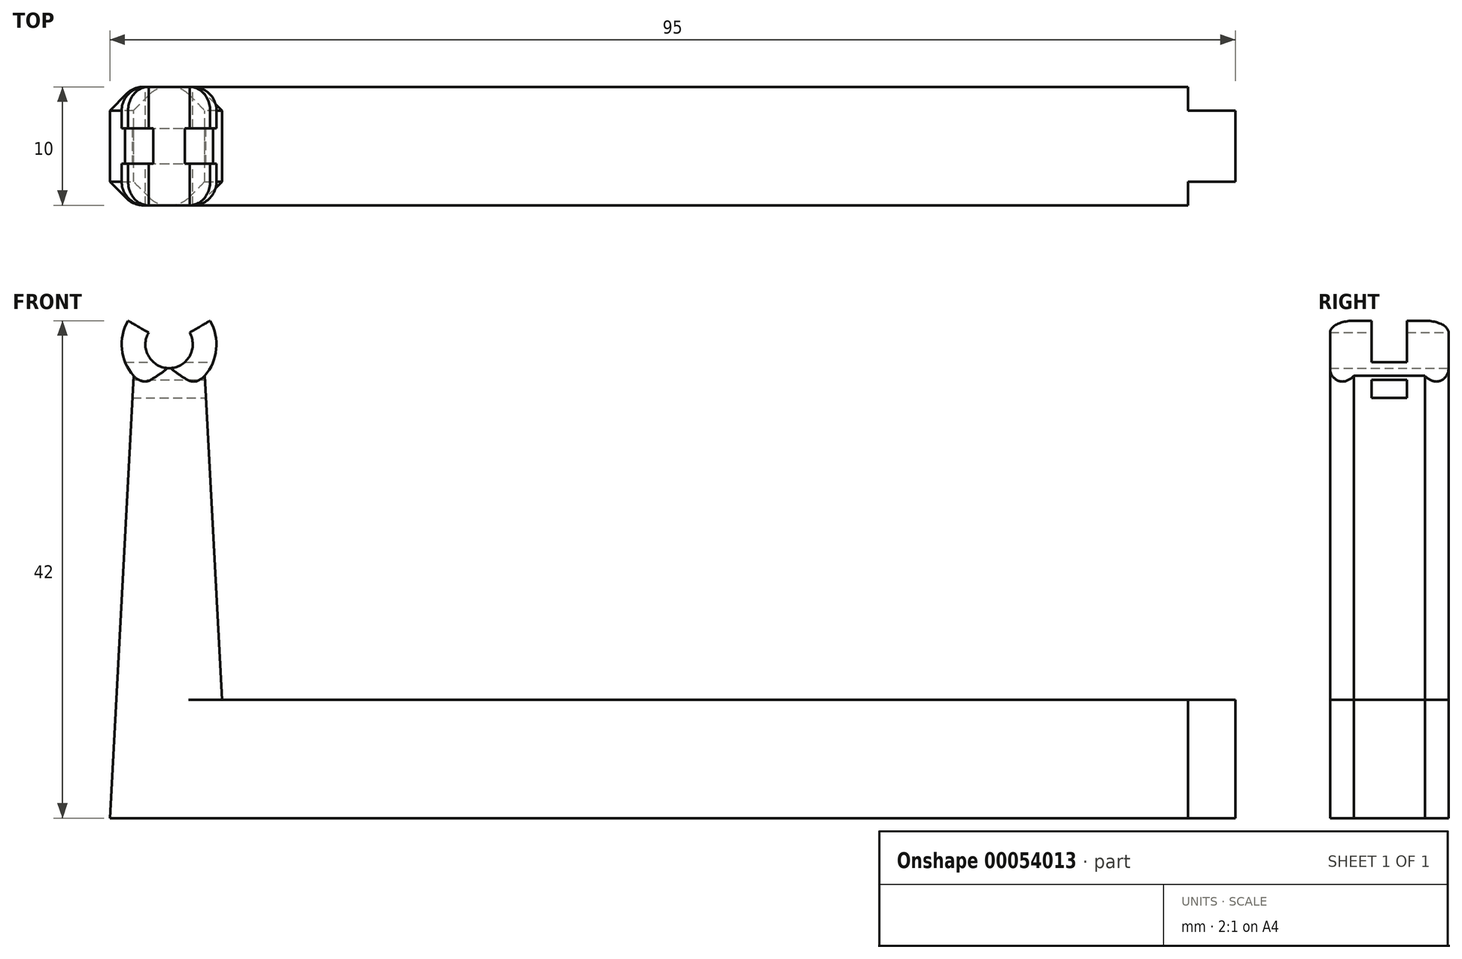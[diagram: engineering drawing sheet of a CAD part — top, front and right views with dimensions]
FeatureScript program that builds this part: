
annotation { "Feature Type Name" : "Feature", "Feature Type Description" : "" }
export const myFeature = defineFeature(function(context is Context, id is Id, definition is map)
    precondition{}
    {
        {
            var Q0;
            Q0=qCreatedBy(makeId("Top.planeOp"),FACE);
            var sketch = newSketch(context, id + "F0", { "sketchPlane" : qUnion([Q0])});
            skLineSegment(sketch, "E0.bottom", {"start": v(-90, 5) * mm, "end": v(-4, 5) * mm});
            skLineSegment(sketch, "E0.top", {"start": v(-90, -5) * mm, "end": v(-4, -5) * mm});
            skLineSegment(sketch, "E0.left", {"start": v(-90, 5) * mm, "end": v(-90, -5) * mm});
            skLineSegment(sketch, "E0.right", {"start": v(-4, 5) * mm, "end": v(-4, 3) * mm});
            skLineSegment(sketch, "E1.bottom", {"start": v(-4, 3) * mm, "end": v(0, 3) * mm});
            skLineSegment(sketch, "E1.top", {"start": v(-4, -3) * mm, "end": v(0, -3) * mm});
            skLineSegment(sketch, "E1.right", {"start": v(0, 3) * mm, "end": v(0, -3) * mm});
            skLineSegment(sketch, "E2.trimOffspring", {"start": v(-4, -3) * mm, "end": v(-4, -5) * mm});
            skSolve(sketch);
        }
        {
            var Q0;
            Q0 = qSketchRegion(id + "F0", true);
            extrude(context, id + "F1", {"entities" : qUnion([Q0]), "depth" : 10 * mm});
        }
        {
            var Q0;
            Q0=qCreatedBy(makeId("Front.planeOp"),FACE);
            var sketch = newSketch(context, id + "F2", { "sketchPlane" : qUnion([Q0])});
            skArc(sketch, "E3", {"start": v(-91.73, 41) * mm, "mid": v(-90, 38) * mm, "end": v(-88.27, 41) * mm});
            skArc(sketch, "E4", {"start": v(-93.46, 42) * mm, "mid": v(-93.98, 39.6) * mm, "end": v(-93, 37.35) * mm});
            skLineSegment(sketch, "E5", {"start": v(-93.46, 42) * mm, "end": v(-91.73, 41) * mm});
            skLineSegment(sketch, "E6.trimOffspring", {"start": v(-88.27, 41) * mm, "end": v(-86.54, 42) * mm});
            skLineSegment(sketch, "E7", {"start": v(-87, 37.35) * mm, "end": v(-85, 0) * mm});
            skLineSegment(sketch, "E8", {"start": v(-85, 0) * mm, "end": v(-95, 0) * mm});
            skLineSegment(sketch, "E9", {"start": v(-95, 0) * mm, "end": v(-93, 37.35) * mm});
            skArc(sketch, "E10.trimOffspring", {"start": v(-87, 37.35) * mm, "mid": v(-86.02, 39.6) * mm, "end": v(-86.54, 42) * mm});
            skLineSegment(sketch, "E11", {"start": v(-90, 40) * mm, "end": v(-90, -15.05) * mm, "construction": true});
            skSolve(sketch);
        }
        {
            var Q0;
            Q0 = qSketchRegion(id + "F2", true);
            extrude(context, id + "F3", {"entities" : qUnion([Q0]), "operationType" : NewBodyOperationType.ADD, "endBound" : BoundingType.SYMMETRIC, "depth" : 10 * mm});
        }
        {
            var Q0;
            Q0=qCreatedBy(makeId("Right.planeOp"),FACE);
            var sketch = newSketch(context, id + "F4", { "sketchPlane" : qUnion([Q0])});
            skLineSegment(sketch, "E12.bottom", {"start": v(-1.5, 37) * mm, "end": v(1.5, 37) * mm});
            skLineSegment(sketch, "E12.top", {"start": v(-1.5, 35.5) * mm, "end": v(1.5, 35.5) * mm});
            skLineSegment(sketch, "E12.left", {"start": v(-1.5, 37) * mm, "end": v(-1.5, 35.5) * mm});
            skLineSegment(sketch, "E12.right", {"start": v(1.5, 37) * mm, "end": v(1.5, 35.5) * mm});
            skLineSegment(sketch, "E13.bottom", {"start": v(1.5, 42) * mm, "end": v(-1.5, 42) * mm});
            skLineSegment(sketch, "E13.top", {"start": v(1.5, 38.5) * mm, "end": v(-1.5, 38.5) * mm});
            skLineSegment(sketch, "E13.left", {"start": v(1.5, 42) * mm, "end": v(1.5, 38.5) * mm});
            skLineSegment(sketch, "E13.right", {"start": v(-1.5, 42) * mm, "end": v(-1.5, 38.5) * mm});
            skSolve(sketch);
        }
        {
            var Q0;
            Q0 = qSketchRegion(id + "F4", true);
            extrude(context, id + "F5", {"entities" : qUnion([Q0]), "operationType" : NewBodyOperationType.REMOVE, "endBound" : BoundingType.THROUGH_ALL, "oppositeDirection" : true, "depth" : 25 * mm});
        }
        {
            var Q0;
            Q0=makeQuery(id+"F3.opExtrude","CAP_EDGE",EDGE,{"disambiguationData":[OSD([sQuery(id+"F2.wireOp",EDGE,"E7")])],"isStart":true});
            var Q1;
            Q1=makeQuery(id+"F3.opExtrude","CAP_EDGE",EDGE,{"disambiguationData":[OSD([sQuery(id+"F2.wireOp",EDGE,"E9")])],"isStart":true});
            var Q2;
            Q2=makeQuery(id+"F3.opExtrude","CAP_EDGE",EDGE,{"disambiguationData":[OSD([sQuery(id+"F2.wireOp",EDGE,"E9")])],"isStart":false});
            var Q3;
            Q3=makeQuery(id+"F3.opExtrude","CAP_EDGE",EDGE,{"disambiguationData":[OSD([sQuery(id+"F2.wireOp",EDGE,"E7")])],"isStart":false});
            chamfer(context, id + "F6", {"entities" : qUnion([Q0, Q1, Q2, Q3]), "width" : 2 * mm, "tangentPropagation" : true});
        }
        {
            var Q0;
            Q0=makeQuery(id+"F3.opExtrude","CAP_EDGE",EDGE,{"disambiguationData":[OSD([sQuery(id+"F2.wireOp",EDGE,"E4")])],"isStart":false});
            var Q1;
            Q1=makeQuery(id+"F3.opExtrude","CAP_EDGE",EDGE,{"disambiguationData":[OSD([sQuery(id+"F2.wireOp",EDGE,"E10.trimOffspring")])],"isStart":false});
            var Q2;
            Q2=makeQuery(id+"F3.opExtrude","CAP_EDGE",EDGE,{"disambiguationData":[OSD([sQuery(id+"F2.wireOp",EDGE,"E4")])],"isStart":true});
            var Q3;
            Q3=makeQuery(id+"F3.opExtrude","CAP_EDGE",EDGE,{"disambiguationData":[OSD([sQuery(id+"F2.wireOp",EDGE,"E10.trimOffspring")])],"isStart":true});
            var Q4;
            {var subQ0=sQuery(id+"F2.wireOp",EDGE,"E9");Q4=makeQuery(id+"F6.opChamfer","BLEND_EDGE",EDGE,{"blendedFrom":[makeQuery(id+"F3.opExtrude","CAP_EDGE",EDGE,{"disambiguationData":[OSD([subQ0])],"isStart":true}),makeQuery(id+"F3.boolean.opBoolean","MERGE",FACE,{"derivedFrom":[makeQuery(id+"F1.opExtrude","SWEPT_FACE",FACE,{"disambiguationData":[OSD([sQuery(id+"F0.wireOp",EDGE,"E0.bottom")])]}),makeQuery(id+"F3.opExtrude","CAP_FACE",FACE,{"disambiguationData":[OSD([sQuery(id+"F2.wireOp",EDGE,"E3"),sQuery(id+"F2.wireOp",EDGE,"E4"),sQuery(id+"F2.wireOp",EDGE,"E5"),sQuery(id+"F2.wireOp",EDGE,"E6.trimOffspring"),sQuery(id+"F2.wireOp",EDGE,"E7"),sQuery(id+"F2.wireOp",EDGE,"E8"),subQ0,sQuery(id+"F2.wireOp",EDGE,"E10.trimOffspring")])],"isStart":true})]})],"blendedInto":[makeQuery(id+"F3.boolean.opBoolean","MERGE",FACE,{"derivedFrom":[makeQuery(id+"F1.opExtrude","SWEPT_FACE",FACE,{"disambiguationData":[OSD([sQuery(id+"F0.wireOp",EDGE,"E0.bottom")])]}),makeQuery(id+"F3.opExtrude","CAP_FACE",FACE,{"disambiguationData":[OSD([sQuery(id+"F2.wireOp",EDGE,"E3"),sQuery(id+"F2.wireOp",EDGE,"E4"),sQuery(id+"F2.wireOp",EDGE,"E5"),sQuery(id+"F2.wireOp",EDGE,"E6.trimOffspring"),sQuery(id+"F2.wireOp",EDGE,"E7"),sQuery(id+"F2.wireOp",EDGE,"E8"),subQ0,sQuery(id+"F2.wireOp",EDGE,"E10.trimOffspring")])],"isStart":true})]})]});}
            var Q5;
            {var subQ0=sQuery(id+"F2.wireOp",EDGE,"E7");Q5=makeQuery(id+"F6.opChamfer","BLEND_EDGE",EDGE,{"blendedFrom":[makeQuery(id+"F3.opExtrude","CAP_EDGE",EDGE,{"disambiguationData":[OSD([subQ0])],"isStart":true}),makeQuery(id+"F3.boolean.opBoolean","MERGE",FACE,{"derivedFrom":[makeQuery(id+"F1.opExtrude","SWEPT_FACE",FACE,{"disambiguationData":[OSD([sQuery(id+"F0.wireOp",EDGE,"E0.bottom")])]}),makeQuery(id+"F3.opExtrude","CAP_FACE",FACE,{"disambiguationData":[OSD([sQuery(id+"F2.wireOp",EDGE,"E3"),sQuery(id+"F2.wireOp",EDGE,"E4"),sQuery(id+"F2.wireOp",EDGE,"E5"),sQuery(id+"F2.wireOp",EDGE,"E6.trimOffspring"),subQ0,sQuery(id+"F2.wireOp",EDGE,"E8"),sQuery(id+"F2.wireOp",EDGE,"E9"),sQuery(id+"F2.wireOp",EDGE,"E10.trimOffspring")])],"isStart":true})]})],"blendedInto":[makeQuery(id+"F3.boolean.opBoolean","MERGE",FACE,{"derivedFrom":[makeQuery(id+"F1.opExtrude","SWEPT_FACE",FACE,{"disambiguationData":[OSD([sQuery(id+"F0.wireOp",EDGE,"E0.bottom")])]}),makeQuery(id+"F3.opExtrude","CAP_FACE",FACE,{"disambiguationData":[OSD([sQuery(id+"F2.wireOp",EDGE,"E3"),sQuery(id+"F2.wireOp",EDGE,"E4"),sQuery(id+"F2.wireOp",EDGE,"E5"),sQuery(id+"F2.wireOp",EDGE,"E6.trimOffspring"),subQ0,sQuery(id+"F2.wireOp",EDGE,"E8"),sQuery(id+"F2.wireOp",EDGE,"E9"),sQuery(id+"F2.wireOp",EDGE,"E10.trimOffspring")])],"isStart":true})]})]});}
            var Q6;
            {var subQ0=sQuery(id+"F2.wireOp",EDGE,"E9");Q6=makeQuery(id+"F6.opChamfer","BLEND_EDGE",EDGE,{"blendedFrom":[makeQuery(id+"F3.opExtrude","CAP_EDGE",EDGE,{"disambiguationData":[OSD([subQ0])],"isStart":false}),makeQuery(id+"F3.boolean.opBoolean","MERGE",FACE,{"derivedFrom":[makeQuery(id+"F1.opExtrude","SWEPT_FACE",FACE,{"disambiguationData":[OSD([sQuery(id+"F0.wireOp",EDGE,"E0.top")])]}),makeQuery(id+"F3.opExtrude","CAP_FACE",FACE,{"disambiguationData":[OSD([sQuery(id+"F2.wireOp",EDGE,"E3"),sQuery(id+"F2.wireOp",EDGE,"E4"),sQuery(id+"F2.wireOp",EDGE,"E5"),sQuery(id+"F2.wireOp",EDGE,"E6.trimOffspring"),sQuery(id+"F2.wireOp",EDGE,"E7"),sQuery(id+"F2.wireOp",EDGE,"E8"),subQ0,sQuery(id+"F2.wireOp",EDGE,"E10.trimOffspring")])],"isStart":false})]})],"blendedInto":[makeQuery(id+"F3.boolean.opBoolean","MERGE",FACE,{"derivedFrom":[makeQuery(id+"F1.opExtrude","SWEPT_FACE",FACE,{"disambiguationData":[OSD([sQuery(id+"F0.wireOp",EDGE,"E0.top")])]}),makeQuery(id+"F3.opExtrude","CAP_FACE",FACE,{"disambiguationData":[OSD([sQuery(id+"F2.wireOp",EDGE,"E3"),sQuery(id+"F2.wireOp",EDGE,"E4"),sQuery(id+"F2.wireOp",EDGE,"E5"),sQuery(id+"F2.wireOp",EDGE,"E6.trimOffspring"),sQuery(id+"F2.wireOp",EDGE,"E7"),sQuery(id+"F2.wireOp",EDGE,"E8"),subQ0,sQuery(id+"F2.wireOp",EDGE,"E10.trimOffspring")])],"isStart":false})]})]});}
            var Q7;
            {var subQ0=sQuery(id+"F2.wireOp",EDGE,"E7");Q7=makeQuery(id+"F6.opChamfer","BLEND_EDGE",EDGE,{"blendedFrom":[makeQuery(id+"F3.opExtrude","CAP_EDGE",EDGE,{"disambiguationData":[OSD([subQ0])],"isStart":false}),makeQuery(id+"F3.boolean.opBoolean","MERGE",FACE,{"derivedFrom":[makeQuery(id+"F1.opExtrude","SWEPT_FACE",FACE,{"disambiguationData":[OSD([sQuery(id+"F0.wireOp",EDGE,"E0.top")])]}),makeQuery(id+"F3.opExtrude","CAP_FACE",FACE,{"disambiguationData":[OSD([sQuery(id+"F2.wireOp",EDGE,"E3"),sQuery(id+"F2.wireOp",EDGE,"E4"),sQuery(id+"F2.wireOp",EDGE,"E5"),sQuery(id+"F2.wireOp",EDGE,"E6.trimOffspring"),subQ0,sQuery(id+"F2.wireOp",EDGE,"E8"),sQuery(id+"F2.wireOp",EDGE,"E9"),sQuery(id+"F2.wireOp",EDGE,"E10.trimOffspring")])],"isStart":false})]})],"blendedInto":[makeQuery(id+"F3.boolean.opBoolean","MERGE",FACE,{"derivedFrom":[makeQuery(id+"F1.opExtrude","SWEPT_FACE",FACE,{"disambiguationData":[OSD([sQuery(id+"F0.wireOp",EDGE,"E0.top")])]}),makeQuery(id+"F3.opExtrude","CAP_FACE",FACE,{"disambiguationData":[OSD([sQuery(id+"F2.wireOp",EDGE,"E3"),sQuery(id+"F2.wireOp",EDGE,"E4"),sQuery(id+"F2.wireOp",EDGE,"E5"),sQuery(id+"F2.wireOp",EDGE,"E6.trimOffspring"),subQ0,sQuery(id+"F2.wireOp",EDGE,"E8"),sQuery(id+"F2.wireOp",EDGE,"E9"),sQuery(id+"F2.wireOp",EDGE,"E10.trimOffspring")])],"isStart":false})]})]});}
            fillet(context, id + "F7", {"entities" : qUnion([Q0, Q1, Q2, Q3, Q4, Q5, Q6, Q7]), "radius" : 2 * mm, "tangentPropagation" : true, "allowEdgeOverflow" : false});
        }
    });
